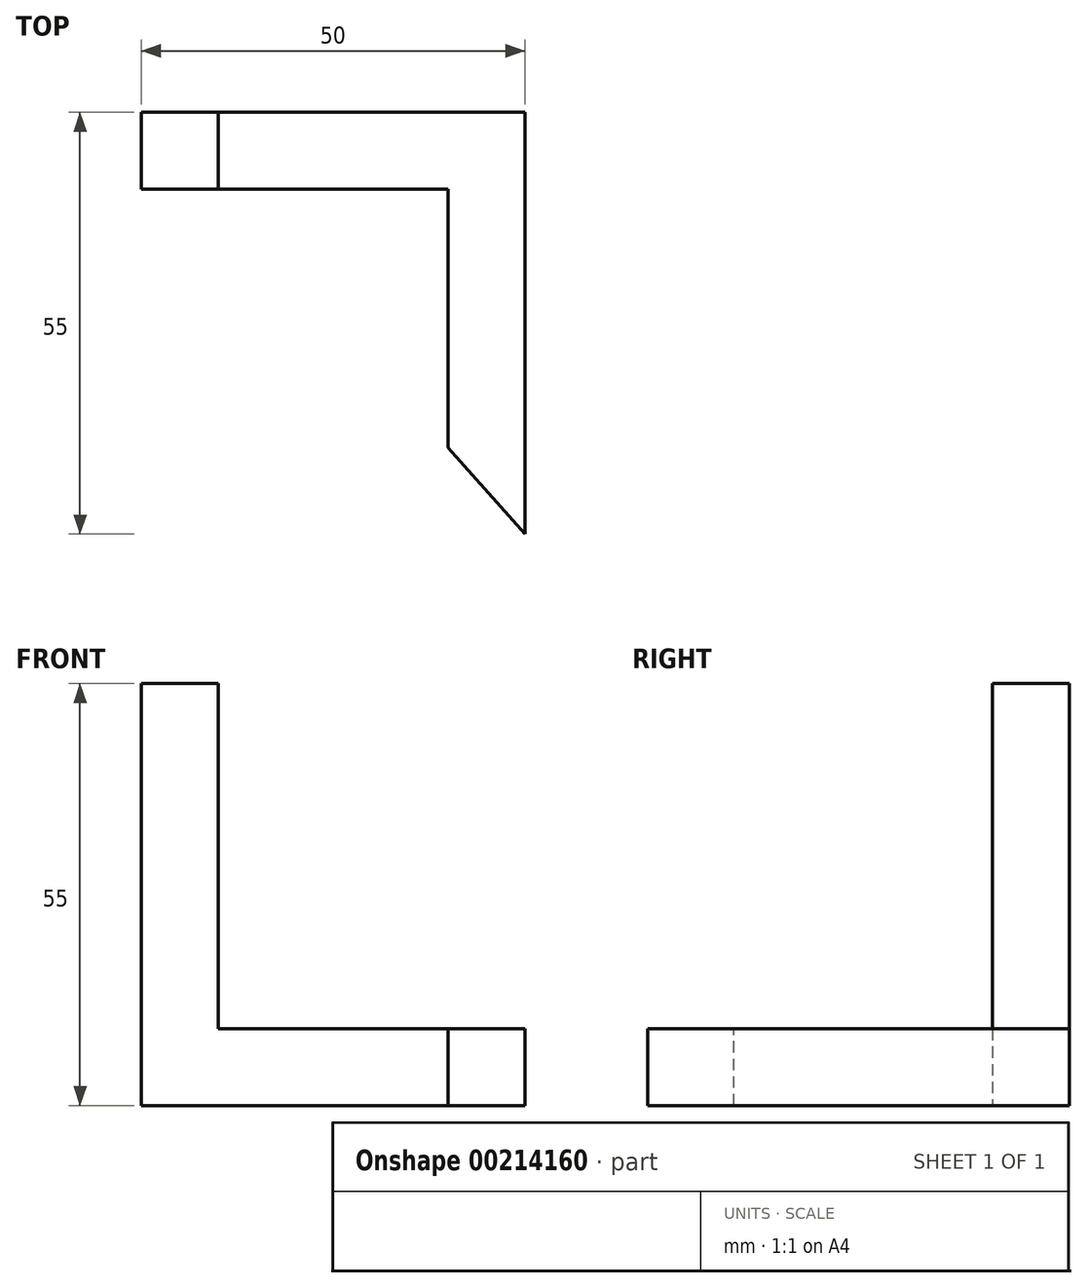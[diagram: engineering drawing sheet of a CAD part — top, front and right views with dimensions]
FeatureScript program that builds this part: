
annotation { "Feature Type Name" : "Feature", "Feature Type Description" : "" }
export const myFeature = defineFeature(function(context is Context, id is Id, definition is map)
    precondition{}
    {
        {
            var Q0;
            Q0=qCreatedBy(makeId("Right.planeOp"),FACE);
            var sketch = newSketch(context, id + "F0", { "sketchPlane" : qUnion([Q0])});
            skCircle(sketch, "E0.cCircle", {"center": v(0, 0) * mm, "radius": 5 * mm, "construction": true});
            skLineSegment(sketch, "E0.0", {"start": v(-5, 5) * mm, "end": v(5, 5) * mm});
            skLineSegment(sketch, "E0.1", {"start": v(5, 5) * mm, "end": v(5, -5) * mm});
            skLineSegment(sketch, "E0.2", {"start": v(5, -5) * mm, "end": v(-5, -5) * mm});
            skLineSegment(sketch, "E0.3", {"start": v(-5, -5) * mm, "end": v(-5, 5) * mm});
            skPoint(sketch, "E0.0.midPoint", {"position": v(0, 5) * mm});
            skSolve(sketch);
        }
        {
            var Q0;
            Q0 = qSketchRegion(id + "F0", true);
            extrude(context, id + "F1", {"entities" : qUnion([Q0]), "depth" : 50 * mm});
        }
        {
            var Q0;
            Q0=qCreatedBy(makeId("Top.planeOp"),FACE);
            var sketch = newSketch(context, id + "F2", { "sketchPlane" : qUnion([Q0])});
            skLineSegment(sketch, "E1.bottom", {"start": v(0, 5) * mm, "end": v(10, 5) * mm});
            skLineSegment(sketch, "E1.top", {"start": v(0, -5) * mm, "end": v(10, -5) * mm});
            skLineSegment(sketch, "E1.left", {"start": v(0, 5) * mm, "end": v(0, -5) * mm});
            skLineSegment(sketch, "E1.right", {"start": v(10, 5) * mm, "end": v(10, -5) * mm});
            skPoint(sketch, "E2.0", {"position": v(0, -5) * mm});
            skPoint(sketch, "E3.0", {"position": v(0, 5) * mm});
            skSolve(sketch);
        }
        {
            var Q0;
            Q0 = qSketchRegion(id + "F2", true);
            extrude(context, id + "F3", {"entities" : qUnion([Q0]), "operationType" : NewBodyOperationType.ADD, "depth" : 50 * mm});
        }
        {
            var Q0;
            Q0=qCreatedBy(makeId("Front.planeOp"),FACE);
            var sketch = newSketch(context, id + "F4", { "sketchPlane" : qUnion([Q0])});
            skLineSegment(sketch, "E4.bottom", {"start": v(40, -5) * mm, "end": v(50, -5) * mm});
            skLineSegment(sketch, "E4.top", {"start": v(40, 5) * mm, "end": v(50, 5) * mm});
            skLineSegment(sketch, "E4.left", {"start": v(40, -5) * mm, "end": v(40, 5) * mm});
            skLineSegment(sketch, "E4.right", {"start": v(50, -5) * mm, "end": v(50, 5) * mm});
            skSolve(sketch);
        }
        {
            var Q0;
            Q0 = qSketchRegion(id + "F4", true);
            extrude(context, id + "F5", {"entities" : qUnion([Q0]), "operationType" : NewBodyOperationType.ADD, "depth" : 50 * mm});
        }
        {
            var Q0;
            Q0=makeQuery(id+"F5.opExtrude","CAP_EDGE",EDGE,{"disambiguationData":[OSD([sQuery(id+"F4.wireOp",EDGE,"E4.left")])],"isStart":false});
            chamfer(context, id + "F6", {"entities" : qUnion([Q0]), "chamferType" : ChamferType.TWO_OFFSETS, "width1" : 11.25 * mm, "oppositeDirection" : false, "width2" : 10 * mm, "tangentPropagation" : true});
        }
    });
